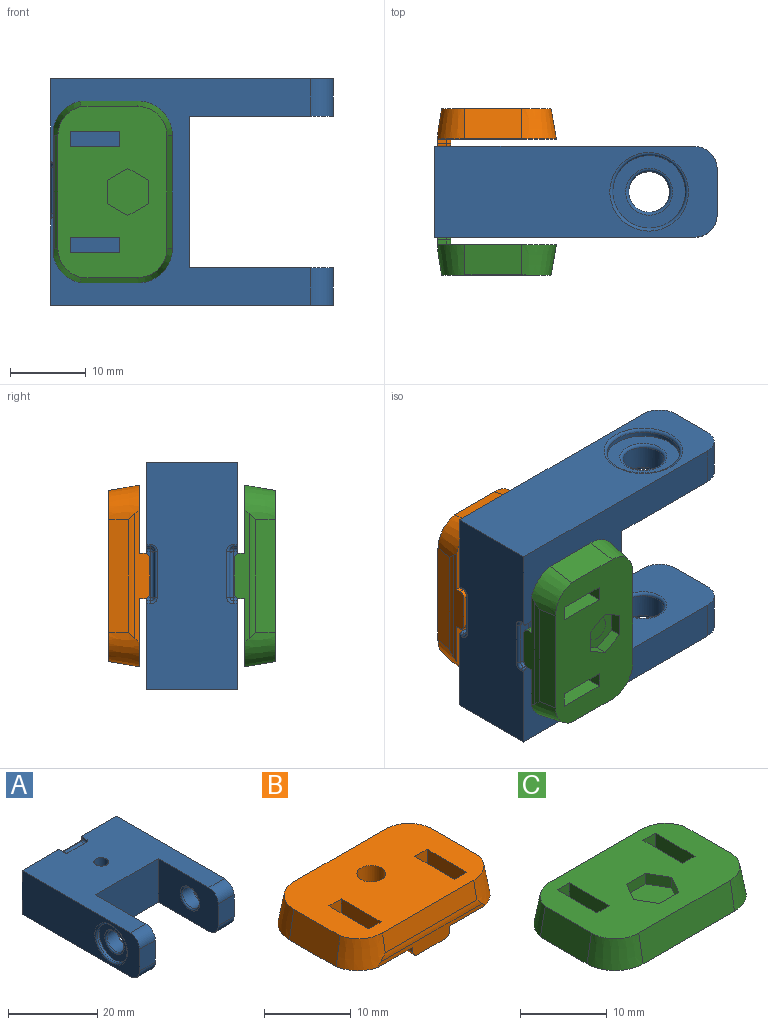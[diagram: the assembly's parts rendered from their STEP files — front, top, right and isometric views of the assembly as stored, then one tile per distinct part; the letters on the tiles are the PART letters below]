
ASSEMBLY  parts=3 mates=2
PART A: 59 faces, bbox 30x37.4x12 mm
  f0: plane 19x12mm, normal (1,0,0), area 193.9mm2, adj f1,f9,f18,f21,f39,f40,f58
  f1: plane 20x12mm, normal (0,-1,0), area 240mm2, adj f0,f3,f21,f40
  f2: plane 37.35x12mm, normal (-1,0,0), area 359.4mm2, adj f7,f12,f18,f21,f39,f40,f58
  f3: plane 19x12mm, normal (-1,0,0), area 193.9mm2, adj f1,f10,f17,f21,f38,f40,f57
  f4: plane 9.6x9.6mm, normal (1,0,0), area 42.2mm2, adj f6,f13
  f5: torus R=5.2mm, axis (-1,0,0), area 19.5mm2, adj f13,f20
  f6: torus R=3.1mm, axis (1,0,0), area 11.2mm2, adj f4,f16
  f7: torus R=5.2mm, axis (1,0,0), area 18.8mm2, adj f2,f15
  f8: torus R=3.1mm, axis (-1,0,0), area 11.2mm2, adj f14,f19
  f9: torus R=3.1mm, axis (-1,0,0), area 11.2mm2, adj f0,f19
  f10: torus R=3.1mm, axis (-1,0,0), area 11.2mm2, adj f3,f16
  f11: cylinder r=1.65mm len=12mm, axis (0,0,1), area 124.4mm2, adj f21,f40
  f12: plane 30x12mm, normal (0,1,0), area 338.6mm2, adj f2,f20,f21,f33,f34,f35,f36,f37
  f13: cylinder r=4.8mm len=9.6mm, axis (-1,0,0), area 18.1mm2, adj f4,f5
  f14: plane 9.6x9.6mm, normal (-1,0,0), area 42.2mm2, adj f8,f15
  f15: cylinder r=4.8mm len=9.6mm, axis (1,0,0), area 18.1mm2, adj f7,f14
  f16: cylinder r=2.7mm len=5.4mm, axis (-1,0,0), area 54.3mm2, adj f6,f10
  f17: plane 6x5mm, normal (0,-1,0), area 30mm2, adj f3,f20,f38,f57
  f18: plane 6x5mm, normal (0,-1,0), area 30mm2, adj f0,f2,f39,f58
  f19: cylinder r=2.7mm len=5.4mm, axis (-1,0,0), area 54.3mm2, adj f8,f9
  f20: plane 37.35x12mm, normal (1,0,0), area 359.4mm2, adj f5,f12,f17,f21,f38,f40,f57
  f21: plane 34.35x30mm, normal (0,0,-1), area 685mm2, adj f0,f1,f2,f3,f11,f12,f20,f23
  f22: plane 6.1x1.5mm, normal (0,0,-1), area 9.1mm2, adj f24,f25,f29,f35
  f23: plane 1.5x0.5mm, normal (1,0,0), area 0.8mm2, adj f21,f25,f28,f33
  f24: cylinder r=0.5mm len=1.5mm, axis (0,1,0), area 1.2mm2, adj f22,f26,f32,f36
  f25: cylinder r=0.5mm len=1.5mm, axis (0,-1,0), area 1.2mm2, adj f22,f23,f31,f34
  f26: plane 1.5x0.5mm, normal (-1,0,0), area 0.8mm2, adj f21,f24,f30,f37
  f27: plane 6.1x0.5mm, normal (0,1,0), area 3mm2, adj f21,f28,f29,f30
  f28: cylinder r=0.5mm len=0.5mm, axis (0,0,1), area 0.4mm2, adj f21,f23,f27,f31
  f29: cylinder r=0.5mm len=6.1mm, axis (1,0,0), area 4.8mm2, adj f22,f27,f31,f32
  f30: cylinder r=0.5mm len=0.5mm, axis (0,0,1), area 0.4mm2, adj f21,f26,f27,f32
  f31: sphere r=0.5mm, area 0.3mm2, adj f25,f28,f29
  f32: sphere r=0.5mm, area 0.5mm2, adj f24,f29,f30
  f33: cylinder r=0.4mm len=0.5mm, axis (0,0,1), area 0.3mm2, adj f12,f21,f23,f34
  f34: torus R=0.9mm, axis (0,-1,0), area 0.6mm2, adj f12,f25,f33,f35
  f35: cylinder r=0.4mm len=6.1mm, axis (1,0,0), area 3.8mm2, adj f12,f22,f34,f36
  f36: torus R=0.9mm, axis (0,-1,0), area 0.6mm2, adj f12,f24,f35,f37
  f37: cylinder r=0.4mm len=0.5mm, axis (0,0,-1), area 0.3mm2, adj f12,f21,f26,f36
  f38: cylinder r=3mm len=5mm, axis (1,0,0), area 23.6mm2, adj f3,f17,f20,f21
  f39: cylinder r=3mm len=5mm, axis (1,0,0), area 23.6mm2, adj f0,f2,f18,f21
  f40: plane 34.35x30mm, normal (0,0,1), area 685mm2, adj f0,f1,f2,f3,f11,f12,f20,f42
  f41: plane 6.1x1.5mm, normal (0,0,1), area 9.1mm2, adj f43,f44,f48,f54
  f42: plane 1.5x0.5mm, normal (1,0,0), area 0.7mm2, adj f40,f44,f47,f52
  f43: cylinder r=0.5mm len=1.5mm, axis (0,1,0), area 1.2mm2, adj f41,f45,f51,f55
  f44: cylinder r=0.5mm len=1.5mm, axis (0,-1,0), area 1.2mm2, adj f41,f42,f50,f53
  f45: plane 1.5x0.5mm, normal (-1,0,0), area 0.8mm2, adj f40,f43,f49,f56
  f46: plane 6.1x0.5mm, normal (0,1,0), area 3mm2, adj f40,f47,f48,f49
  f47: cylinder r=0.5mm len=0.5mm, axis (0,0,-1), area 0.4mm2, adj f40,f42,f46,f50
  f48: cylinder r=0.5mm len=6.1mm, axis (1,0,0), area 4.8mm2, adj f41,f46,f50,f51
  f49: cylinder r=0.5mm len=0.5mm, axis (0,0,-1), area 0.4mm2, adj f40,f45,f46,f51
  f50: sphere r=0.5mm, area 0.3mm2, adj f44,f47,f48
  f51: sphere r=0.5mm, area 0.5mm2, adj f43,f48,f49
  f52: cylinder r=0.4mm len=0.5mm, axis (0,0,-1), area 0.3mm2, adj f12,f40,f42,f53
  f53: torus R=0.9mm, axis (0,-1,0), area 0.6mm2, adj f12,f44,f52,f54
  f54: cylinder r=0.4mm len=6.1mm, axis (1,0,0), area 3.8mm2, adj f12,f41,f53,f55
  f55: torus R=0.9mm, axis (0,-1,0), area 0.6mm2, adj f12,f43,f54,f56
  f56: cylinder r=0.4mm len=0.5mm, axis (0,0,1), area 0.3mm2, adj f12,f40,f45,f55
  f57: cylinder r=3mm len=5mm, axis (1,0,0), area 23.6mm2, adj f3,f17,f20,f40
  f58: cylinder r=3mm len=5mm, axis (1,0,0), area 23.6mm2, adj f0,f2,f18,f40
PART B: 56 faces, bbox 24.1x15.9x5.4 mm
  f0: bspline ~0.75x0.75mm, area 0.7mm2, adj f1,f9,f10,f55
  f1: cylinder r=0.5mm len=4.5mm, axis (-1,0,0), area 3.5mm2, adj f0,f11,f13,f55
  f2: cone r=4.24mm half-angle=10deg, axis (0,0,-1), area 22.7mm2, adj f3,f4,f17,f18,f19,f20
  f3: plane 24.04x15.67mm, normal (0,0,-1), area 238.8mm2, adj f2,f4,f5,f6,f7,f8,f9,f12
  f4: plane 7.61x4mm, normal (-0.98,0,0.17), area 30.7mm2, adj f2,f3,f20,f21
  f5: plane 14.9x4mm, normal (0,0.98,0.17), area 60.5mm2, adj f3,f20,f21,f22
  f6: plane 7.61x4mm, normal (0.98,0,0.17), area 30.7mm2, adj f3,f7,f20,f22
  f7: cone r=4.24mm half-angle=10deg, axis (0,0,-1), area 22.7mm2, adj f3,f6,f17,f18,f19,f20
  f8: plane 6.5x4mm, normal (1,0,0), area 26mm2, adj f3,f20,f51,f53
  f9: cylinder r=0.5mm len=0.65mm, axis (0,0,-1), area 0.5mm2, adj f0,f3,f16,f55
  f10: cylinder r=0.75mm len=1.2mm, axis (0,1,0), area 1.4mm2, adj f0,f13,f16,f18
  f11: bspline ~0.75x0.75mm, area 0.7mm2, adj f1,f12,f14,f55
  f12: cylinder r=0.5mm len=0.65mm, axis (0,0,-1), area 0.5mm2, adj f3,f11,f15,f55
  f13: plane 4.5x1.2mm, normal (0,0,-1), area 5.4mm2, adj f1,f10,f14,f18
  f14: cylinder r=0.75mm len=1.2mm, axis (0,-1,0), area 1.4mm2, adj f11,f13,f15,f18
  f15: plane 1.2x0.65mm, normal (-1,0,0), area 0.8mm2, adj f3,f12,f14,f18
  f16: plane 1.2x0.65mm, normal (1,0,0), area 0.8mm2, adj f3,f9,f10,f18
  f17: cylinder r=5mm len=16.57mm, axis (-1,0,0), area 13.7mm2, adj f2,f7,f18,f19
  f18: plane 17.48x2mm, normal (0,-1,0), area 17.7mm2, adj f2,f3,f7,f10,f13,f14,f15,f16
  f19: plane 14.9x2.57mm, normal (0,-0.98,0.17), area 38.9mm2, adj f2,f7,f17,f20
  f20: plane 22.62x14.44mm, normal (0,0,1), area 279.6mm2, adj f2,f4,f5,f6,f7,f8,f19,f21
  f21: cone r=4.24mm half-angle=10deg, axis (0,0,-1), area 26.9mm2, adj f3,f4,f5,f20
  f22: cone r=4.24mm half-angle=10deg, axis (0,0,-1), area 26.9mm2, adj f3,f5,f6,f20
  f23: plane 6.5x1mm, normal (0,0,-1), area 6.5mm2, adj f29,f37,f38,f51
  f24: plane 6.5x1mm, normal (0,0,-1), area 6.5mm2, adj f25,f26,f38,f51
  f25: plane 6.5x0.4mm, normal (1,0,0), area 2.6mm2, adj f24,f38,f44,f51
  f26: plane 6.5x0.4mm, normal (-1,0,0), area 2.6mm2, adj f24,f38,f46,f51
  f27: plane 6.5x1mm, normal (0,0,-1), area 6.5mm2, adj f28,f29,f38,f51
  f28: plane 6.5x0.4mm, normal (1,0,0), area 2.6mm2, adj f27,f38,f46,f51
  f29: plane 6.5x0.4mm, normal (-1,0,0), area 2.6mm2, adj f23,f27,f38,f51
  f30: plane 6.5x1mm, normal (0,0,-1), area 6.5mm2, adj f31,f32,f51,f53
  f31: plane 6.5x0.4mm, normal (-1,0,0), area 2.6mm2, adj f30,f51,f53,f54
  f32: plane 6.5x0.4mm, normal (1,0,0), area 2.6mm2, adj f30,f45,f51,f53
  f33: plane 6.03x1mm, normal (0,0,-1), area 6mm2, adj f34,f35,f42,f51
  f34: plane 6.03x0.4mm, normal (1,0,0), area 2.4mm2, adj f33,f42,f43,f51
  f35: plane 6.03x0.4mm, normal (-1,0,0), area 2.4mm2, adj f33,f42,f44,f51
  f36: plane 6.5x0.5mm, normal (0,0,-1), area 3.2mm2, adj f37,f38,f48,f51
  f37: plane 6.5x0.4mm, normal (1,0,0), area 2.6mm2, adj f23,f36,f38,f51
  f38: plane 6.77x4mm, normal (0,-1,0), area 10.9mm2, adj f3,f20,f23,f24,f25,f26,f27,f28
  f39: plane 6.5x1mm, normal (0,0,-1), area 6.5mm2, adj f40,f51,f52,f53
  f40: plane 6.5x0.4mm, normal (-1,0,0), area 2.6mm2, adj f39,f43,f51,f53
  f41: plane 6.5x4mm, normal (-1,0,0), area 26mm2, adj f3,f20,f38,f51
  f42: cylinder r=1.65mm len=4mm, axis (0,0,-1), area 40mm2, adj f3,f20,f33,f34,f35,f38,f43,f44
  f43: plane 6.5x1mm, normal (0,0,-1), area 6.3mm2, adj f34,f40,f42,f51,f53
  f44: plane 6.5x1mm, normal (0,0,-1), area 6.3mm2, adj f25,f35,f38,f42,f51
  f45: plane 6.5x1mm, normal (0,0,-1), area 6.5mm2, adj f32,f50,f51,f53
  f46: plane 6.5x1mm, normal (0,0,-1), area 6.5mm2, adj f26,f28,f38,f51
  f47: plane 6.5x3.2mm, normal (-1,0,0), area 20.8mm2, adj f20,f49,f51,f53
  f48: plane 6.5x3.2mm, normal (1,0,0), area 20.8mm2, adj f20,f36,f38,f51
  f49: plane 6.5x0.5mm, normal (0,0,-1), area 3.2mm2, adj f47,f50,f51,f53
  f50: plane 6.5x0.4mm, normal (-1,0,0), area 2.6mm2, adj f45,f49,f51,f53
  f51: plane 16x4mm, normal (0,1,0), area 23.2mm2, adj f3,f8,f20,f23,f24,f25,f26,f27
  f52: plane 6.5x0.4mm, normal (1,0,0), area 2.6mm2, adj f39,f51,f53,f54
  f53: plane 6.77x4mm, normal (0,-1,0), area 10.9mm2, adj f3,f8,f20,f30,f31,f32,f39,f40
  f54: plane 6.5x1mm, normal (0,0,-1), area 6.5mm2, adj f31,f51,f52,f53
  f55: plane 5x0.9mm, normal (0,1,0), area 4.5mm2, adj f0,f1,f3,f9,f11,f12
PART C: 64 faces, bbox 24.1x15.9x5.4 mm
  f0: cylinder r=0.5mm len=0.65mm, axis (0,0,-1), area 0.5mm2, adj f1,f3,f31,f63
  f1: bspline ~0.75x0.75mm, area 0.7mm2, adj f0,f2,f30,f31
  f2: cylinder r=0.75mm len=1.2mm, axis (0,-1,0), area 1.4mm2, adj f1,f3,f9,f25
  f3: plane 1.2x0.65mm, normal (1,0,0), area 0.8mm2, adj f0,f2,f25,f63
  f4: cylinder r=0.75mm len=1.2mm, axis (0,1,0), area 1.4mm2, adj f9,f25,f27,f29
  f5: plane 6.5x4mm, normal (1,0,0), area 26mm2, adj f24,f33,f61,f63
  f6: cone r=4.24mm half-angle=10deg, axis (0,0,-1), area 22.7mm2, adj f10,f24,f25,f26,f62,f63
  f7: plane 7.61x4mm, normal (-0.98,0,0.17), area 30.7mm2, adj f8,f24,f35,f63
  f8: cone r=4.24mm half-angle=10deg, axis (0,0,-1), area 22.7mm2, adj f7,f10,f24,f25,f26,f63
  f9: plane 4.5x1.2mm, normal (0,0,-1), area 5.4mm2, adj f2,f4,f25,f30
  f10: plane 14.9x2.57mm, normal (0,0.98,0.17), area 38.9mm2, adj f6,f8,f24,f26
  f11: plane 3.12x1.5mm, normal (0,-1,0), area 4.7mm2, adj f12,f16,f17,f24
  f12: plane 2.7x1.56mm, normal (0.87,-0.5,0), area 4.7mm2, adj f11,f13,f17,f24
  f13: plane 2.7x1.56mm, normal (0.87,0.5,0), area 4.7mm2, adj f12,f14,f17,f24
  f14: plane 3.12x1.5mm, normal (0,1,0), area 4.7mm2, adj f13,f15,f17,f24
  f15: plane 2.7x1.56mm, normal (-0.87,0.5,0), area 4.7mm2, adj f14,f16,f17,f24
  f16: plane 2.7x1.56mm, normal (-0.87,-0.5,0), area 4.7mm2, adj f11,f15,f17,f24
  f17: plane 6.24x5.4mm, normal (0,0,1), area 25.3mm2, adj f11,f12,f13,f14,f15,f16
  f18: plane 3.3x3.3mm, normal (0,0,-1), area 8.6mm2, adj f19
  f19: cylinder r=1.65mm len=3.3mm, axis (0,0,-1), area 23.4mm2, adj f18,f33,f47,f48,f49,f51,f54,f55
  f20: plane 6.5x0.4mm, normal (-1,0,0), area 2.6mm2, adj f33,f56,f60,f61
  f21: plane 6.5x0.5mm, normal (0,0,-1), area 3.2mm2, adj f50,f51,f59,f61
  f22: plane 6.5x0.4mm, normal (1,0,0), area 2.6mm2, adj f39,f51,f55,f61
  f23: plane 6.5x4mm, normal (-1,0,0), area 26mm2, adj f24,f51,f61,f63
  f24: plane 22.62x14.44mm, normal (0,0,1), area 262.9mm2, adj f5,f6,f7,f8,f10,f11,f12,f13
  f25: plane 17.48x2mm, normal (0,1,0), area 17.7mm2, adj f2,f3,f4,f6,f8,f9,f26,f27
  f26: cylinder r=5mm len=16.57mm, axis (-1,0,0), area 13.7mm2, adj f6,f8,f10,f25
  f27: plane 1.2x0.65mm, normal (-1,0,0), area 0.8mm2, adj f4,f25,f28,f63
  f28: cylinder r=0.5mm len=0.65mm, axis (0,0,-1), area 0.5mm2, adj f27,f29,f31,f63
  f29: bspline ~0.75x0.75mm, area 0.7mm2, adj f4,f28,f30,f31
  f30: cylinder r=0.5mm len=4.5mm, axis (-1,0,0), area 3.5mm2, adj f1,f9,f29,f31
  f31: plane 5x0.9mm, normal (0,-1,0), area 4.5mm2, adj f0,f1,f28,f29,f30,f63
  f32: plane 6.5x1mm, normal (0,0,-1), area 6.5mm2, adj f33,f34,f45,f61
  f33: plane 6.77x4mm, normal (0,1,0), area 10.9mm2, adj f5,f19,f20,f24,f32,f34,f44,f45
  f34: plane 6.5x0.4mm, normal (1,0,0), area 2.6mm2, adj f32,f33,f52,f61
  f35: cone r=4.24mm half-angle=10deg, axis (0,0,-1), area 26.9mm2, adj f7,f24,f36,f63
  f36: plane 14.9x4mm, normal (0,-0.98,0.17), area 60.5mm2, adj f24,f35,f37,f63
  f37: cone r=4.24mm half-angle=10deg, axis (0,0,-1), area 26.9mm2, adj f24,f36,f62,f63
  f38: plane 6.5x1mm, normal (0,0,-1), area 6.5mm2, adj f43,f50,f51,f61
  f39: plane 6.5x1mm, normal (0,0,-1), area 6.5mm2, adj f22,f40,f51,f61
  f40: plane 6.5x0.4mm, normal (-1,0,0), area 2.6mm2, adj f39,f51,f57,f61
  f41: plane 6.5x1mm, normal (0,0,-1), area 6.5mm2, adj f42,f43,f51,f61
  f42: plane 6.5x0.4mm, normal (1,0,0), area 2.6mm2, adj f41,f51,f57,f61
  f43: plane 6.5x0.4mm, normal (-1,0,0), area 2.6mm2, adj f38,f41,f51,f61
  f44: plane 6.5x1mm, normal (0,0,-1), area 6.5mm2, adj f33,f45,f46,f61
  f45: plane 6.5x0.4mm, normal (-1,0,0), area 2.6mm2, adj f32,f33,f44,f61
  f46: plane 6.5x0.4mm, normal (1,0,0), area 2.6mm2, adj f33,f44,f56,f61
  f47: plane 6.03x1mm, normal (0,0,-1), area 6mm2, adj f19,f48,f49,f61
  f48: plane 6.03x0.4mm, normal (1,0,0), area 2.4mm2, adj f19,f47,f54,f61
  f49: plane 6.03x0.4mm, normal (-1,0,0), area 2.4mm2, adj f19,f47,f55,f61
  f50: plane 6.5x0.4mm, normal (1,0,0), area 2.6mm2, adj f21,f38,f51,f61
  f51: plane 6.77x4mm, normal (0,1,0), area 10.9mm2, adj f19,f21,f22,f23,f24,f38,f39,f40
  f52: plane 6.5x1mm, normal (0,0,-1), area 6.5mm2, adj f33,f34,f53,f61
  f53: plane 6.5x0.4mm, normal (-1,0,0), area 2.6mm2, adj f33,f52,f54,f61
  f54: plane 6.5x1mm, normal (0,0,-1), area 6.3mm2, adj f19,f33,f48,f53,f61
  f55: plane 6.5x1mm, normal (0,0,-1), area 6.3mm2, adj f19,f22,f49,f51,f61
  f56: plane 6.5x1mm, normal (0,0,-1), area 6.5mm2, adj f20,f33,f46,f61
  f57: plane 6.5x1mm, normal (0,0,-1), area 6.5mm2, adj f40,f42,f51,f61
  f58: plane 6.5x3.2mm, normal (-1,0,0), area 20.8mm2, adj f24,f33,f60,f61
  f59: plane 6.5x3.2mm, normal (1,0,0), area 20.8mm2, adj f21,f24,f51,f61
  f60: plane 6.5x0.5mm, normal (0,0,-1), area 3.2mm2, adj f20,f33,f58,f61
  f61: plane 16x4mm, normal (0,-1,0), area 23.2mm2, adj f5,f20,f21,f22,f23,f24,f32,f34
  f62: plane 7.61x4mm, normal (0.98,0,0.17), area 30.7mm2, adj f6,f24,f37,f63
  f63: plane 24.04x15.67mm, normal (0,0,-1), area 238.8mm2, adj f0,f3,f5,f6,f7,f8,f19,f23
PLACE A rot(axis=(0.58,-0.58,0.58),120deg) t=(-6.15,-44.1,-25)mm
PLACE B rot(axis=(-0.58,-0.58,-0.58),120deg) t=(-22.24,-15.5,0)mm
PLACE C rot(axis=(0.58,-0.58,0.58),120deg) t=(-22.24,15.5,0)mm
MATE fastened C.f19 <-> A.f11  axis (0,1,0) through (-8.15,-7,0)mm
MATE fastened B.f42 <-> A.f11  axis (0,-1,0) through (-8.15,7,0)mm
